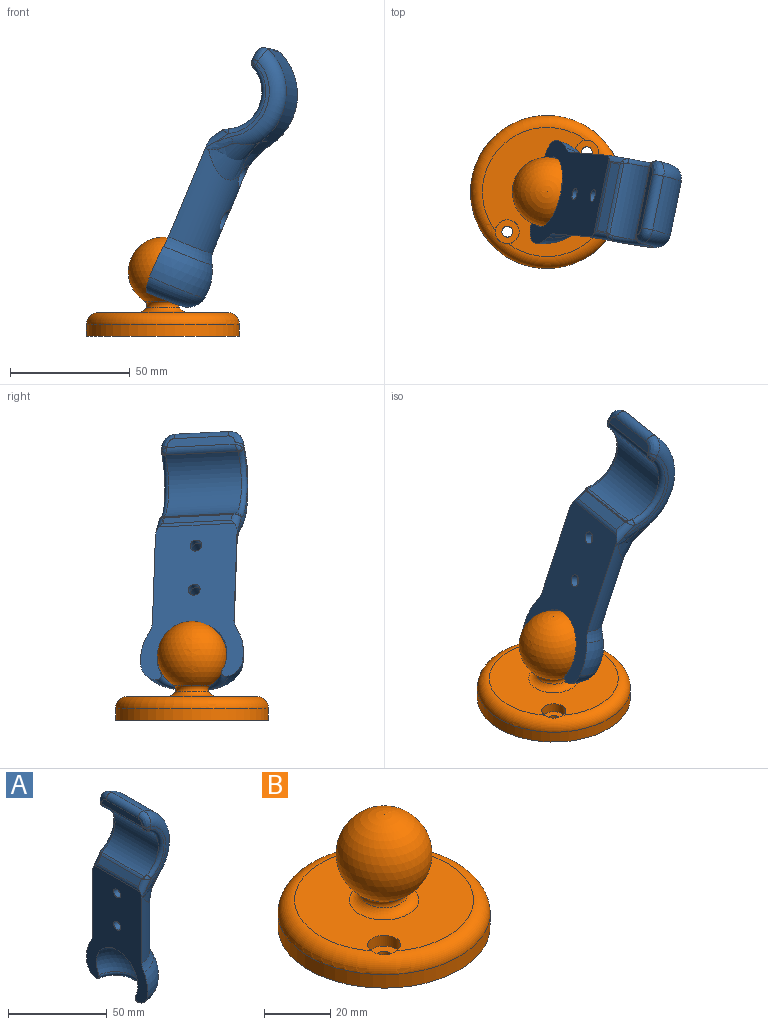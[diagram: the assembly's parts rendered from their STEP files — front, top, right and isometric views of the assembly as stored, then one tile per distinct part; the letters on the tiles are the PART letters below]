
ASSEMBLY  parts=2 mates=1
PART A: 47 faces, bbox 28.1x49.2x115.8 mm
  f0: plane 9.5x9.5mm, normal (1,0,0), area 51.2mm2, adj f1,f46
  f1: cylinder r=2.5mm len=5mm, axis (1,0,0), area 55mm2, adj f0,f2
  f2: plane 69.72x44.28mm, normal (-1,0,0), area 1889.4mm2, adj f1,f3,f35,f36,f37,f38,f39,f40
  f3: cylinder r=2.5mm len=5mm, axis (1,0,0), area 55mm2, adj f2,f4
  f4: plane 9.5x9.5mm, normal (1,0,0), area 51.2mm2, adj f3,f5
  f5: cylinder r=4.75mm len=11.9mm, axis (-1,0,0), area 354.4mm2, adj f4,f6,f33,f34,f42
  f6: bspline ~20.69x19.03mm, area 255.2mm2, adj f5,f7,f34,f36,f42
  f7: torus R=19mm, axis (0,-1,0), area 434mm2, adj f6,f8,f31,f32,f36
  f8: plane 38.66x14.97mm, normal (0,-1,0), area 64.7mm2, adj f7,f9,f30,f35,f36
  f9: cylinder r=3mm len=3mm, axis (0,0,-1), area 5.5mm2, adj f8,f10,f28,f29,f31
  f10: bspline ~2.81x2.81mm, area 3.4mm2, adj f9,f11,f29
  f11: cylinder r=3mm len=30.8mm, axis (0,1,0), area 100.8mm2, adj f10,f12,f27,f28
  f12: cylinder r=15.5mm len=31mm, axis (0,1,0), area 1104.7mm2, adj f11,f13,f19,f21,f25,f26,f29,f30
  f13: torus R=17.5mm, axis (0,-1,0), area 110.8mm2, adj f12,f14,f19,f26
  f14: plane 38.66x14.97mm, normal (0,1,0), area 64.7mm2, adj f13,f15,f18,f43,f44
  f15: torus R=19mm, axis (0,-1,0), area 434mm2, adj f14,f16,f32,f33,f43
  f16: bspline ~9.13x7.77mm, area 44.3mm2, adj f15,f17,f18,f28
  f17: cylinder r=3mm len=23mm, axis (0,1,0), area 134.1mm2, adj f16,f28,f31,f32
  f18: cylinder r=3mm len=3mm, axis (0,0,1), area 5.5mm2, adj f14,f16,f26,f27,f28
  f19: bspline ~3.99x2.98mm, area 5.5mm2, adj f12,f13,f20,f44
  f20: bspline ~1.75x1.47mm, area 0.8mm2, adj f19,f21,f44
  f21: cylinder r=3mm len=30.07mm, axis (0,1,0), area 49.8mm2, adj f12,f20,f22,f23,f24
  f22: bspline ~0.97x0.7mm, area 0.1mm2, adj f21,f35
  f23: plane 29x3.67mm, normal (-0.82,0,0.58), area 130.5mm2, adj f21,f35,f44,f45
  f24: bspline ~1.59x1.34mm, area 0.5mm2, adj f21,f25,f35
  f25: bspline ~3.99x2.98mm, area 5.5mm2, adj f12,f24,f30,f35
  f26: bspline ~2.65x2.29mm, area 2.8mm2, adj f12,f13,f18,f27
  f27: bspline ~2.81x2.81mm, area 3.4mm2, adj f11,f18,f26
  f28: plane 29x3.81mm, normal (-1,0,0), area 106.4mm2, adj f9,f11,f16,f17,f18,f31
  f29: bspline ~2.77x2.36mm, area 2.8mm2, adj f9,f10,f12,f30
  f30: torus R=17.5mm, axis (0,-1,0), area 110.8mm2, adj f8,f12,f25,f29
  f31: bspline ~8.03x7.78mm, area 44.3mm2, adj f7,f9,f17,f28
  f32: cylinder r=25mm len=36.93mm, axis (0,1,0), area 1002.5mm2, adj f7,f15,f17,f34
  f33: bspline ~20.69x19.03mm, area 255.2mm2, adj f5,f15,f34,f42,f43
  f34: bspline ~28.7x18.97mm, area 259.2mm2, adj f5,f6,f32,f33
  f35: cylinder r=3mm len=10.93mm, axis (0.58,0,0.82), area 36.3mm2, adj f2,f8,f22,f23,f24,f25,f36,f45
  f36: bspline ~12.24x8.82mm, area 32.9mm2, adj f2,f6,f7,f8,f35,f42
  f37: sphere r=15mm, area 950.1mm2, adj f2,f38
  f38: torus R=14.95mm, axis (0,0,-1), area 180mm2, adj f2,f37,f39
  f39: torus R=13.83mm, axis (0,0,1), area 560.3mm2, adj f2,f38,f40
  f40: sphere r=22mm, area 927.9mm2, adj f2,f39,f41
  f41: torus R=36.8mm, axis (0,0,-1), area 259.1mm2, adj f2,f40,f42
  f42: cylinder r=17.5mm len=40.18mm, axis (0,0,-1), area 1669.9mm2, adj f2,f5,f6,f33,f36,f41,f43,f46
  f43: bspline ~13.43x9.31mm, area 32.9mm2, adj f2,f14,f15,f33,f42,f44
  f44: cylinder r=3mm len=10.93mm, axis (0.58,0,0.82), area 36.2mm2, adj f2,f14,f19,f20,f23,f43,f45
  f45: cylinder r=3mm len=32.46mm, axis (0,1,0), area 56.7mm2, adj f2,f23,f35,f44
  f46: cylinder r=4.75mm len=12.5mm, axis (-1,0,0), area 373.1mm2, adj f0,f42
PART B: 13 faces, bbox 69.3x69.3x41.5 mm
  f0: cylinder r=2.25mm len=6mm, axis (0,0,-1), area 84.8mm2, adj f4,f8
  f1: cylinder r=2.25mm len=6mm, axis (0,0,-1), area 84.8mm2, adj f4,f6
  f2: cylinder r=32mm len=64mm, axis (0,0,-1), area 1005.3mm2, adj f4,f10
  f3: plane 54x54mm, normal (0,0,1), area 1802.8mm2, adj f5,f7,f10,f11
  f4: plane 64x64mm, normal (0,0,-1), area 3185.2mm2, adj f0,f1,f2
  f5: cylinder r=5mm len=10mm, axis (0,0,1), area 124.6mm2, adj f3,f6,f10
  f6: plane 10x10mm, normal (0,0,1), area 62.6mm2, adj f1,f5
  f7: cylinder r=5mm len=10mm, axis (0,0,1), area 124.6mm2, adj f3,f8,f10
  f8: plane 10x10mm, normal (0,0,1), area 62.6mm2, adj f0,f7
  f9: sphere r=14.5mm, area 2440.6mm2, adj f12
  f10: torus R=27mm, axis (0,0,1), area 1473.3mm2, adj f2,f3,f5,f7
  f11: torus R=10.5mm, axis (0,0,1), area 227.8mm2, adj f3,f12
  f12: torus R=8.76mm, axis (0,0,-1), area 134.2mm2, adj f9,f11
PLACE A rot(axis=(-0.02,0.89,-0.46),25.6deg) t=(32.69,-5.2,10.52)mm
PLACE B rot(axis=(0,0,1),180deg) t=(28.29,-5.02,-30.9)mm fixed
MATE ball B.f12 <-> A.f2  axis (0,0,1) through (28.29,-5.02,-3.9)mm
